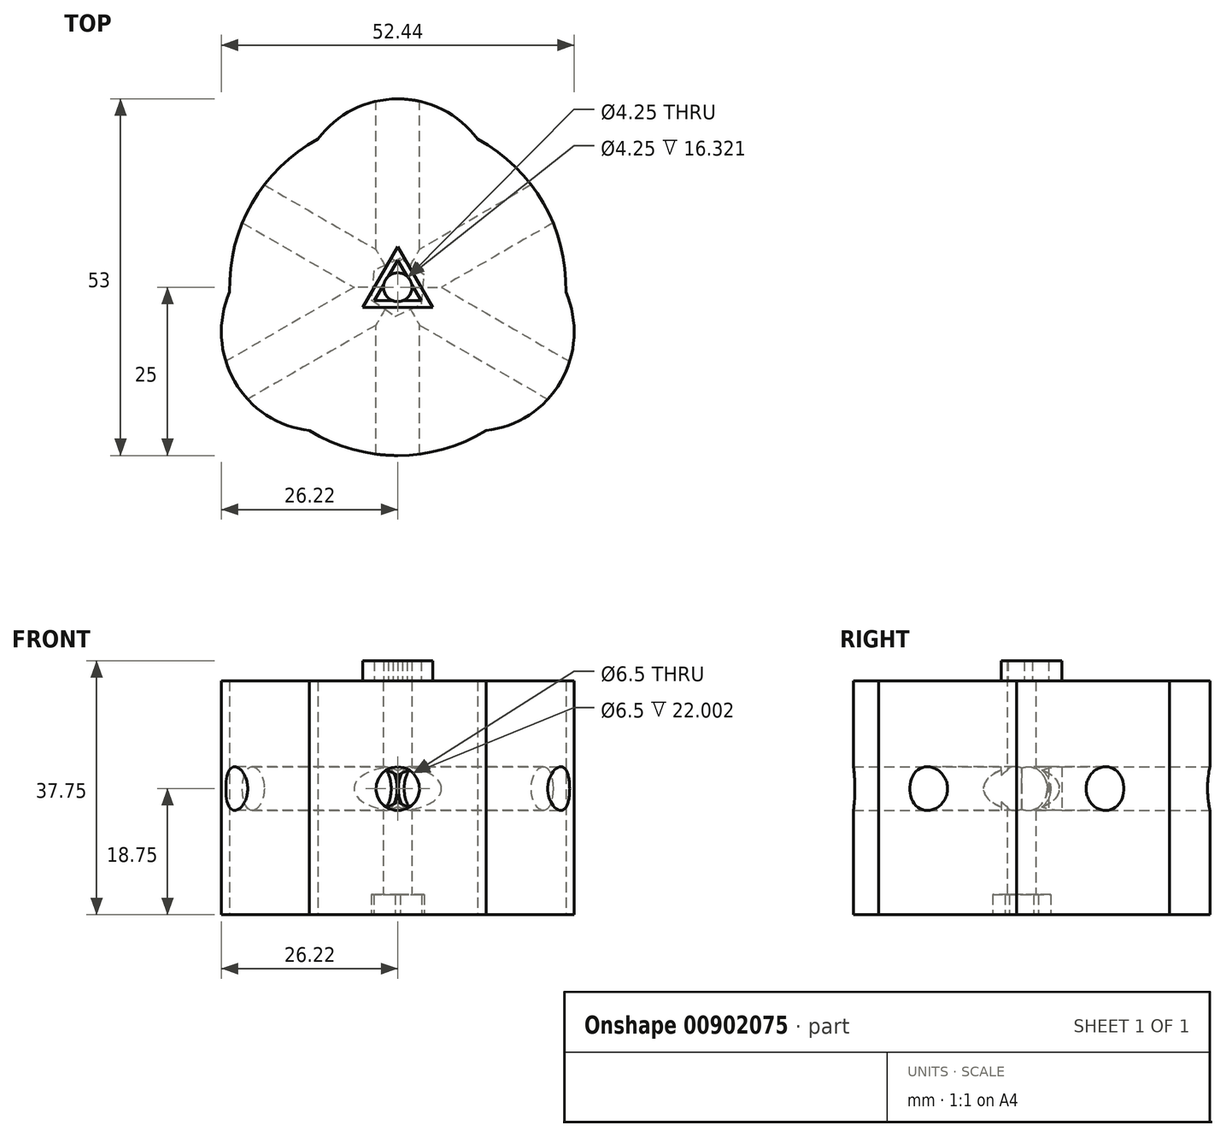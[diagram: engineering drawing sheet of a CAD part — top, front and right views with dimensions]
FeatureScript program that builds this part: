
annotation { "Feature Type Name" : "Feature", "Feature Type Description" : "" }
export const myFeature = defineFeature(function(context is Context, id is Id, definition is map)
    precondition{}
    {
        {
            var Q0;
            Q0=qCreatedBy(makeId("Top.planeOp"),FACE);
            var sketch = newSketch(context, id + "F0", { "sketchPlane" : qUnion([Q0])});
            skCircle(sketch, "E0", {"center": v(0, 0) * mm, "radius": 25 * mm});
            skPoint(sketch, "E1", {"position": v(-11.87, 22) * mm});
            skPoint(sketch, "E2.MirrorP", {"position": v(11.87, 22) * mm});
            skArc(sketch, "E3", {"start": v(11.87, 22) * mm, "mid": v(0, 28) * mm, "end": v(-11.87, 22) * mm});
            skArc(sketch, "E4.1.0", {"start": v(-24.99, -0.72) * mm, "mid": v(-24.25, -14) * mm, "end": v(-13.12, -21.28) * mm});
            skArc(sketch, "E4.2.0", {"start": v(13.12, -21.28) * mm, "mid": v(24.25, -14) * mm, "end": v(24.99, -0.72) * mm});
            skSolve(sketch);
        }
        {
            var Q0;
            Q0=makeQuery(id+"F0.imprint","IMPRINT",FACE,{"disambiguationData":[TD([[makeQuery(id+"F0.imprint","IMPRINT",EDGE,{"derivedFrom":sQuery(id+"F0.wireOp",EDGE,"iPbp3OPt-Og0e-h1Yw-MaBf-0AZW6OAXDtnJ")}),-1.0]])]});
            var Q1;
            {var subQ0=sQuery(id+"F0.wireOp",EDGE,"E3");Q1=makeQuery(id+"F0.imprint","IMPRINT",FACE,{"disambiguationData":[TD([[makeQuery(id+"F0.imprint","IMPRINT",EDGE,{"derivedFrom":subQ0}),1.0]])]});}
            var Q2;
            {var subQ0=sQuery(id+"F0.wireOp",EDGE,"E4.1.0");Q2=makeQuery(id+"F0.imprint","IMPRINT",FACE,{"disambiguationData":[TD([[makeQuery(id+"F0.imprint","IMPRINT",EDGE,{"derivedFrom":subQ0}),1.0]])]});}
            var Q3;
            {var subQ0=sQuery(id+"F0.wireOp",EDGE,"E4.2.0");Q3=makeQuery(id+"F0.imprint","IMPRINT",FACE,{"disambiguationData":[TD([[makeQuery(id+"F0.imprint","IMPRINT",EDGE,{"derivedFrom":subQ0}),1.0]])]});}
            var Q4;
            Q4=makeQuery(id+"F0.imprint","IMPRINT",FACE,{"disambiguationData":[TD([[makeQuery(id+"F0.imprint","IMPRINT",EDGE,{"derivedFrom":sQuery(id+"F0.wireOp",EDGE,"6CoMubdr-rplY-xLew-Zasb-LncCztSGb2TN")}),-1.0]])]});
            var Q5;
            {var subQ1=sQuery(id+"F0.wireOp",EDGE,"E0");var subQ4=sQuery(id+"F0.wireOp",EDGE,"E3");var subQ6=makeQuery(id+"F0.imprint","INTERSECT",VERTEX,{"disambiguationData":[OD(0.0)],"derivedFrom":[subQ1,subQ4]});Q5=makeQuery(id+"F0.imprint","IMPRINT",FACE,{"disambiguationData":[TD([[makeQuery(id+"F0.imprint","IMPRINT",EDGE,{"disambiguationData":[TD([[subQ6,1.0]])],"derivedFrom":subQ1}),1.0]])]});}
            extrude(context, id + "F1", {"entities" : qUnion([Q0, Q1, Q2, Q3, Q4, Q5]), "depth" : 22 * mm, "offsetDistance" : 25 * mm});
        }
        {
            var Q0;
            Q0=qCreatedBy(makeId("Front.planeOp"),FACE);
            cPlane(context, id + "F2", {"entities" : qUnion([Q0]), "cplaneType" : CPlaneType.OFFSET, "offset" : 0 * mm, "width" : 150 * mm, "height" : 150 * mm});
        }
        {
            var Q0;
            Q0=qCreatedBy(id+"F2.planeOp",FACE);
            var sketch = newSketch(context, id + "F3", { "sketchPlane" : qUnion([Q0])});
            skPoint(sketch, "E5", {"position": v(0, 6) * mm});
            skCircle(sketch, "E6", {"center": v(0, 6) * mm, "radius": 3.25 * mm});
            skSolve(sketch);
        }
        {
            var Q0;
            Q0=makeQuery(id+"F3.imprint","IMPRINT",FACE,{"disambiguationData":[TD([[makeQuery(id+"F3.imprint","IMPRINT",EDGE,{"derivedFrom":sQuery(id+"F3.wireOp",EDGE,"E6")}),1.0]])]});
            extrude(context, id + "F4", {"entities" : qUnion([Q0]), "operationType" : NewBodyOperationType.REMOVE, "depth" : 50 * mm, "offsetDistance" : 25 * mm, "hasSecondDirection" : true, "secondDirectionOppositeDirection" : true, "secondDirectionDepth" : 50 * mm});
        }
        {
            var Q0;
            Q0=qCreatedBy(makeId("Top.planeOp"),FACE);
            var sketch = newSketch(context, id + "F5", { "sketchPlane" : qUnion([Q0])});
            skCircle(sketch, "E7.cCircle", {"center": v(0, 0) * mm, "radius": 3 * mm, "construction": true});
            skLineSegment(sketch, "E7.0", {"start": v(5.2, -3) * mm, "end": v(-5.2, -3) * mm});
            skLineSegment(sketch, "E7.1", {"start": v(-5.2, -3) * mm, "end": v(0, 6) * mm});
            skLineSegment(sketch, "E7.2", {"start": v(0, 6) * mm, "end": v(5.2, -3) * mm});
            skPoint(sketch, "E7.0.midPoint", {"position": v(0, -3) * mm});
            skCircle(sketch, "E8.cCircle", {"center": v(0, 0) * mm, "radius": 2 * mm, "construction": true});
            skLineSegment(sketch, "E8.0", {"start": v(3.46, -2) * mm, "end": v(-3.46, -2) * mm});
            skLineSegment(sketch, "E8.1", {"start": v(-3.46, -2) * mm, "end": v(0, 4) * mm});
            skLineSegment(sketch, "E8.2", {"start": v(0, 4) * mm, "end": v(3.46, -2) * mm});
            skPoint(sketch, "E8.0.midPoint", {"position": v(0, -2) * mm});
            skSolve(sketch);
        }
        {
            var Q0;
            Q0=makeQuery(id+"F5.imprint","IMPRINT",FACE,{"disambiguationData":[TD([[makeQuery(id+"F5.imprint","IMPRINT",EDGE,{"derivedFrom":sQuery(id+"F5.wireOp",EDGE,"E7.0")}),-1.0]])]});
            extrude(context, id + "F6", {"entities" : qUnion([Q0]), "depth" : 25 * mm, "offsetDistance" : 25 * mm});
        }
        {
            var Q0;
            Q0=makeQuery(id+"F6.opExtrude","SWEPT_FACE",FACE,{"disambiguationData":[OSD([sQuery(id+"F5.wireOp",EDGE,"E7.1")])]});
            var sketch = newSketch(context, id + "F7", { "sketchPlane" : qUnion([Q0])});
            skCircle(sketch, "E9", {"center": v(0, 6) * mm, "radius": 3.25 * mm});
            skSolve(sketch);
        }
        {
            var Q0;
            Q0=makeQuery(id+"F7.imprint","IMPRINT",FACE,{"disambiguationData":[TD([[makeQuery(id+"F7.imprint","IMPRINT",EDGE,{"derivedFrom":sQuery(id+"F7.wireOp",EDGE,"E9")}),1.0]])]});
            extrude(context, id + "F8", {"entities" : qUnion([Q0]), "operationType" : NewBodyOperationType.REMOVE, "depth" : 25 * mm, "offsetDistance" : 25 * mm, "hasSecondDirection" : true, "secondDirectionOppositeDirection" : true, "secondDirectionDepth" : 40 * mm});
        }
        {
            var Q0;
            Q0=makeQuery(id+"F6.opExtrude","SWEPT_FACE",FACE,{"disambiguationData":[OSD([sQuery(id+"F5.wireOp",EDGE,"E7.2")])]});
            var sketch = newSketch(context, id + "F9", { "sketchPlane" : qUnion([Q0])});
            skCircle(sketch, "E10", {"center": v(0, 6) * mm, "radius": 3.25 * mm});
            skSolve(sketch);
        }
        {
            var Q0;
            Q0=makeQuery(id+"F9.imprint","IMPRINT",FACE,{"disambiguationData":[TD([[makeQuery(id+"F9.imprint","IMPRINT",EDGE,{"derivedFrom":sQuery(id+"F9.wireOp",EDGE,"E10")}),1.0]])]});
            extrude(context, id + "F10", {"entities" : qUnion([Q0]), "operationType" : NewBodyOperationType.REMOVE, "depth" : 25 * mm, "offsetDistance" : 25 * mm, "hasSecondDirection" : true, "secondDirectionOppositeDirection" : true, "secondDirectionDepth" : 40 * mm});
        }
        {
            var Q0;
            {var subQ1=sQuery(id+"F0.wireOp",EDGE,"E0");var subQ4=sQuery(id+"F0.wireOp",EDGE,"E3");var subQ6=makeQuery(id+"F0.imprint","INTERSECT",VERTEX,{"disambiguationData":[OD(0.0)],"derivedFrom":[subQ1,subQ4]});Q0=makeQuery(id+"F0.imprint","IMPRINT",FACE,{"disambiguationData":[TD([[makeQuery(id+"F0.imprint","IMPRINT",EDGE,{"disambiguationData":[TD([[subQ6,1.0]])],"derivedFrom":subQ1}),1.0]])]});}
            var Q1;
            {var subQ0=sQuery(id+"F0.wireOp",EDGE,"E3");Q1=makeQuery(id+"F0.imprint","IMPRINT",FACE,{"disambiguationData":[TD([[makeQuery(id+"F0.imprint","IMPRINT",EDGE,{"derivedFrom":subQ0}),1.0]])]});}
            var Q2;
            {var subQ0=sQuery(id+"F0.wireOp",EDGE,"E4.2.0");Q2=makeQuery(id+"F0.imprint","IMPRINT",FACE,{"disambiguationData":[TD([[makeQuery(id+"F0.imprint","IMPRINT",EDGE,{"derivedFrom":subQ0}),1.0]])]});}
            var Q3;
            {var subQ0=sQuery(id+"F0.wireOp",EDGE,"E4.1.0");Q3=makeQuery(id+"F0.imprint","IMPRINT",FACE,{"disambiguationData":[TD([[makeQuery(id+"F0.imprint","IMPRINT",EDGE,{"derivedFrom":subQ0}),1.0]])]});}
            extrude(context, id + "F11", {"entities" : qUnion([Q0, Q1, Q2, Q3]), "operationType" : NewBodyOperationType.ADD, "oppositeDirection" : true, "depth" : 13.75 * mm, "offsetDistance" : 25 * mm});
        }
        {
            var Q0;
            Q0=qCreatedBy(makeId("Front.planeOp"),FACE);
            var sketch = newSketch(context, id + "F12", { "sketchPlane" : qUnion([Q0])});
            skLineSegment(sketch, "E11.0", {"start": v(-13.12, -13.75) * mm, "end": v(13.12, -13.75) * mm});
            skLineSegment(sketch, "E12", {"start": v(13.12, -13.75) * mm, "end": v(63.12, -13.75) * mm});
            skLineSegment(sketch, "E13.MirrorCS", {"start": v(-13.12, -13.75) * mm, "end": v(-63.12, -13.75) * mm});
            skLineSegment(sketch, "E14", {"start": v(63.12, -13.75) * mm, "end": v(63.12, -12.75) * mm});
            skLineSegment(sketch, "E15", {"start": v(63.12, -12.75) * mm, "end": v(0, -12.75) * mm});
            skLineSegment(sketch, "E16.MirrorCS", {"start": v(-63.12, -13.75) * mm, "end": v(-63.12, -12.75) * mm});
            skLineSegment(sketch, "E17.MirrorCS", {"start": v(-63.12, -12.75) * mm, "end": v(0, -12.75) * mm});
            skSolve(sketch);
        }
        {
            var Q0;
            Q0=makeQuery(id+"F12.imprint","IMPRINT",FACE,{"disambiguationData":[TD([[makeQuery(id+"F12.imprint","IMPRINT",EDGE,{"derivedFrom":sQuery(id+"F12.wireOp",EDGE,"E11.0")}),1.0]])]});
            extrude(context, id + "F13", {"entities" : qUnion([Q0]), "operationType" : NewBodyOperationType.REMOVE, "oppositeDirection" : true, "depth" : 250 * mm, "offsetDistance" : 25 * mm, "hasSecondDirection" : true, "secondDirectionOppositeDirection" : false, "secondDirectionDepth" : 250 * mm});
        }
        {
            var Q0;
            Q0=makeQuery(id+"F13.boolean.opBoolean","COPY",FACE,{"derivedFrom":makeQuery(id+"F13.opExtrude","SWEPT_FACE",FACE,{"disambiguationData":[OSD([sQuery(id+"F12.wireOp",EDGE,"E15"),sQuery(id+"F12.wireOp",EDGE,"E17.MirrorCS")])]})});
            var sketch = newSketch(context, id + "F14", { "sketchPlane" : qUnion([Q0])});
            skCircle(sketch, "E18", {"center": v(0, 0) * mm, "radius": 2.12 * mm});
            skCircle(sketch, "E19.cCircle", {"center": v(0, 0) * mm, "radius": 3.75 * mm, "construction": true});
            skLineSegment(sketch, "E19.0", {"start": v(3.93, -1.82) * mm, "end": v(0.39, -4.31) * mm});
            skLineSegment(sketch, "E19.1", {"start": v(0.39, -4.31) * mm, "end": v(-3.54, -2.5) * mm});
            skLineSegment(sketch, "E19.2", {"start": v(-3.54, -2.5) * mm, "end": v(-3.93, 1.82) * mm});
            skLineSegment(sketch, "E19.3", {"start": v(-3.93, 1.82) * mm, "end": v(-0.39, 4.31) * mm});
            skLineSegment(sketch, "E19.4", {"start": v(-0.39, 4.31) * mm, "end": v(3.54, 2.5) * mm});
            skLineSegment(sketch, "E19.5", {"start": v(3.54, 2.5) * mm, "end": v(3.93, -1.82) * mm});
            skPoint(sketch, "E19.0.midPoint", {"position": v(2.16, -3.07) * mm});
            skSolve(sketch);
        }
        {
            var Q0;
            Q0=makeQuery(id+"F14.imprint","IMPRINT",FACE,{"disambiguationData":[TD([[makeQuery(id+"F14.imprint","IMPRINT",EDGE,{"derivedFrom":sQuery(id+"F14.wireOp",EDGE,"E18")}),1.0]])]});
            extrude(context, id + "F15", {"entities" : qUnion([Q0]), "operationType" : NewBodyOperationType.REMOVE, "oppositeDirection" : true, "depth" : 100 * mm, "offsetDistance" : 25 * mm});
        }
        {
            var Q0;
            Q0=makeQuery(id+"F14.imprint","IMPRINT",FACE,{"disambiguationData":[TD([[makeQuery(id+"F14.imprint","IMPRINT",EDGE,{"derivedFrom":sQuery(id+"F14.wireOp",EDGE,"E18")}),-1.0]])]});
            extrude(context, id + "F16", {"entities" : qUnion([Q0]), "operationType" : NewBodyOperationType.REMOVE, "oppositeDirection" : true, "depth" : 3 * mm, "offsetDistance" : 25 * mm});
        }
    });
